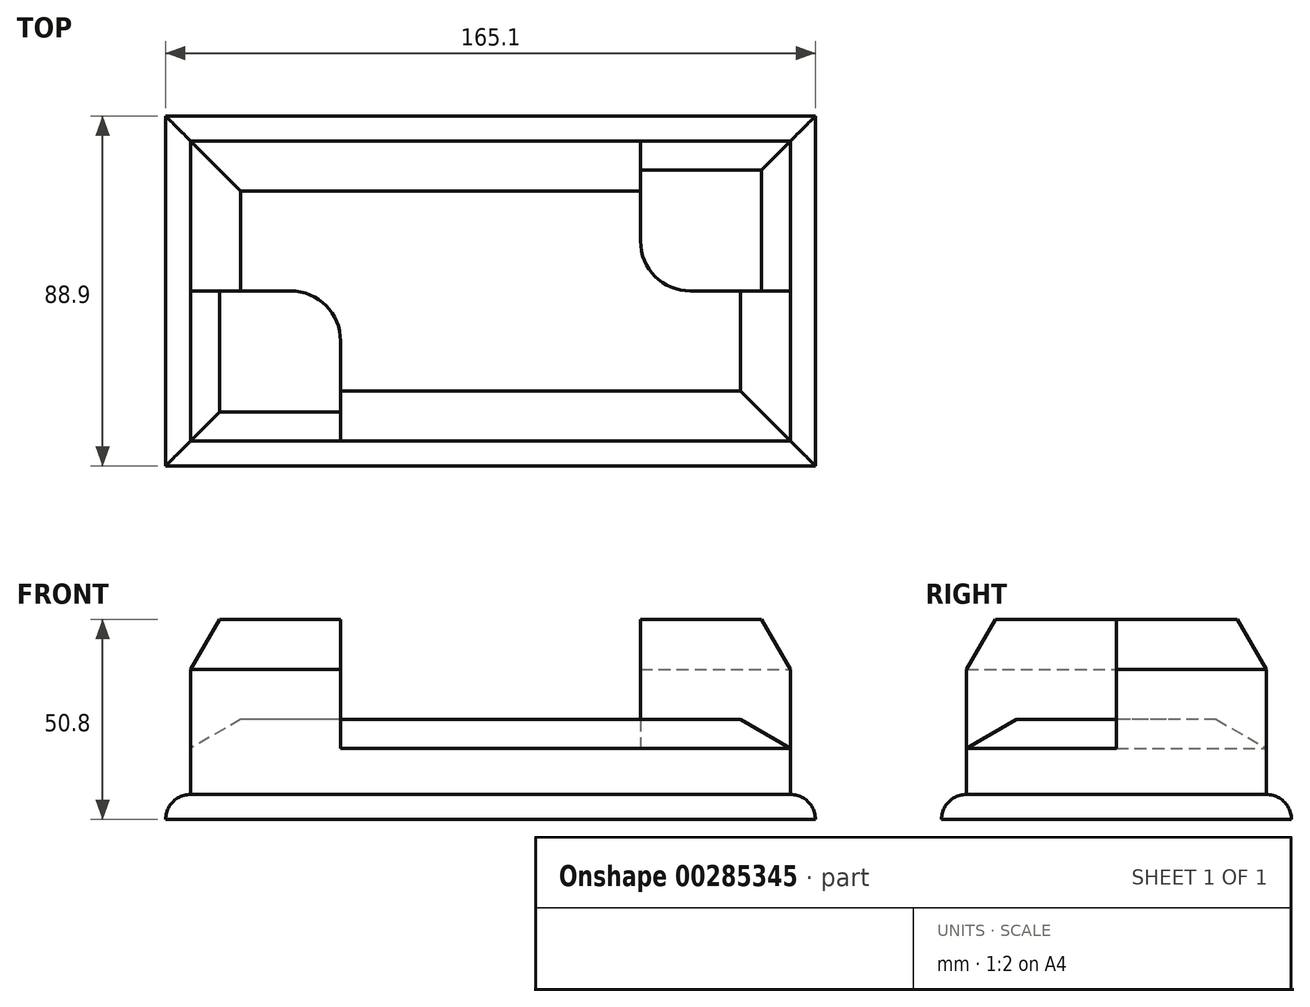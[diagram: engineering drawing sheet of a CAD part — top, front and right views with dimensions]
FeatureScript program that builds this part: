
annotation { "Feature Type Name" : "Feature", "Feature Type Description" : "" }
export const myFeature = defineFeature(function(context is Context, id is Id, definition is map)
    precondition{}
    {
        {
            var Q0;
            Q0=qCreatedBy(makeId("Top.planeOp"),FACE);
            var sketch = newSketch(context, id + "F0", { "sketchPlane" : qUnion([Q0])});
            skLineSegment(sketch, "E0.bottom", {"start": v(-61.87, 51.4) * mm, "end": v(90.53, 51.4) * mm});
            skLineSegment(sketch, "E0.top", {"start": v(-61.87, -24.8) * mm, "end": v(90.53, -24.8) * mm});
            skLineSegment(sketch, "E0.left", {"start": v(-61.87, 51.4) * mm, "end": v(-61.87, -24.8) * mm});
            skLineSegment(sketch, "E0.right", {"start": v(90.53, 51.4) * mm, "end": v(90.53, -24.8) * mm});
            skLineSegment(sketch, "E1.bottom", {"start": v(-36.47, 13.3) * mm, "end": v(-61.87, 13.3) * mm});
            skLineSegment(sketch, "E1.left", {"start": v(-23.77, 0.6) * mm, "end": v(-23.77, -24.8) * mm});
            skLineSegment(sketch, "E2.bottom", {"start": v(-68.22, 57.74) * mm, "end": v(96.88, 57.74) * mm});
            skLineSegment(sketch, "E2.top", {"start": v(-68.22, -31.16) * mm, "end": v(96.88, -31.16) * mm});
            skLineSegment(sketch, "E2.left", {"start": v(-68.22, 57.74) * mm, "end": v(-68.22, -31.16) * mm});
            skLineSegment(sketch, "E2.right", {"start": v(96.88, 57.74) * mm, "end": v(96.88, -31.16) * mm});
            skLineSegment(sketch, "E3.top", {"start": v(90.53, 13.3) * mm, "end": v(65.13, 13.3) * mm});
            skLineSegment(sketch, "E3.right", {"start": v(52.43, 51.4) * mm, "end": v(52.43, 26) * mm});
            skPoint(sketch, "E4.visualSharp", {"position": v(-23.77, 13.3) * mm});
            skArc(sketch, "E4.filletArc", {"start": v(-23.77, 0.6) * mm, "mid": v(-27.5, 9.57) * mm, "end": v(-36.47, 13.3) * mm});
            skPoint(sketch, "E5.visualSharp", {"position": v(52.43, 13.3) * mm});
            skArc(sketch, "E5.filletArc", {"start": v(52.43, 26) * mm, "mid": v(56.15, 17.01) * mm, "end": v(65.13, 13.3) * mm});
            skSolve(sketch);
        }
        {
            var Q0;
            {var subQ7=sQuery(id+"F0.wireOp",EDGE,"E1.bottom");Q0=makeQuery(id+"F0.imprint","IMPRINT",FACE,{"disambiguationData":[TD([[makeQuery(id+"F0.imprint","IMPRINT",EDGE,{"derivedFrom":subQ7}),-1.0]])]});}
            extrude(context, id + "F1", {"entities" : qUnion([Q0]), "depth" : 25.4 * mm});
        }
        {
            var Q0;
            Q0=makeQuery(id+"F0.imprint","IMPRINT",FACE,{"disambiguationData":[TD([[makeQuery(id+"F0.imprint","IMPRINT",EDGE,{"derivedFrom":sQuery(id+"F0.wireOp",EDGE,"E2.bottom")}),-1.0]])]});
            extrude(context, id + "F2", {"entities" : qUnion([Q0]), "operationType" : NewBodyOperationType.ADD, "depth" : 6.35 * mm});
        }
        {
            var Q0;
            {var subQ1=sQuery(id+"F0.wireOp",EDGE,"E1.bottom");Q0=makeQuery(id+"F0.imprint","IMPRINT",FACE,{"disambiguationData":[TD([[makeQuery(id+"F0.imprint","IMPRINT",EDGE,{"derivedFrom":subQ1}),1.0]])]});}
            var Q1;
            {var subQ1=sQuery(id+"F0.wireOp",EDGE,"E3.top");Q1=makeQuery(id+"F0.imprint","IMPRINT",FACE,{"disambiguationData":[TD([[makeQuery(id+"F0.imprint","IMPRINT",EDGE,{"derivedFrom":subQ1}),-1.0]])]});}
            extrude(context, id + "F3", {"entities" : qUnion([Q0, Q1]), "operationType" : NewBodyOperationType.ADD, "depth" : 50.8 * mm});
        }
        {
            var Q0;
            Q0=makeQuery(id+"F3.opExtrude","CAP_EDGE",EDGE,{"disambiguationData":[OSD([sQuery(id+"F0.wireOp",EDGE,"E0.right")])],"isStart":false});
            var Q1;
            Q1=makeQuery(id+"F3.opExtrude","CAP_EDGE",EDGE,{"disambiguationData":[OSD([sQuery(id+"F0.wireOp",EDGE,"E0.bottom")])],"isStart":false});
            chamfer(context, id + "F4", {"entities" : qUnion([Q0, Q1]), "chamferType" : ChamferType.OFFSET_ANGLE, "width" : 12.7 * mm, "oppositeDirection" : false, "angle" : 30 * degree, "tangentPropagation" : true});
        }
        {
            var Q0;
            Q0=makeQuery(id+"F3.opExtrude","CAP_EDGE",EDGE,{"disambiguationData":[OSD([sQuery(id+"F0.wireOp",EDGE,"E0.left")])],"isStart":false});
            var Q1;
            Q1=makeQuery(id+"F3.opExtrude","CAP_EDGE",EDGE,{"disambiguationData":[OSD([sQuery(id+"F0.wireOp",EDGE,"E0.top")])],"isStart":false});
            chamfer(context, id + "F5", {"entities" : qUnion([Q0, Q1]), "chamferType" : ChamferType.OFFSET_ANGLE, "width" : 12.7 * mm, "oppositeDirection" : true, "angle" : 30 * degree, "tangentPropagation" : true});
        }
        {
            var Q0;
            Q0=makeQuery(id+"F1.opExtrude","CAP_EDGE",EDGE,{"disambiguationData":[OSD([sQuery(id+"F0.wireOp",EDGE,"E0.left")])],"isStart":false});
            var Q1;
            Q1=makeQuery(id+"F1.opExtrude","CAP_EDGE",EDGE,{"disambiguationData":[OSD([sQuery(id+"F0.wireOp",EDGE,"E0.bottom")])],"isStart":false});
            var Q2;
            Q2=makeQuery(id+"F1.opExtrude","CAP_EDGE",EDGE,{"disambiguationData":[OSD([sQuery(id+"F0.wireOp",EDGE,"E0.right")])],"isStart":false});
            var Q3;
            Q3=makeQuery(id+"F1.opExtrude","CAP_EDGE",EDGE,{"disambiguationData":[OSD([sQuery(id+"F0.wireOp",EDGE,"E0.top")])],"isStart":false});
            chamfer(context, id + "F6", {"entities" : qUnion([Q0, Q1, Q2, Q3]), "chamferType" : ChamferType.OFFSET_ANGLE, "width" : 12.7 * mm, "oppositeDirection" : false, "angle" : 30 * degree, "tangentPropagation" : true});
        }
        {
            var Q0;
            Q0=makeQuery(id+"F2.opExtrude","CAP_EDGE",EDGE,{"disambiguationData":[OSD([sQuery(id+"F0.wireOp",EDGE,"E2.right")])],"isStart":false});
            var Q1;
            Q1=makeQuery(id+"F2.opExtrude","CAP_EDGE",EDGE,{"disambiguationData":[OSD([sQuery(id+"F0.wireOp",EDGE,"E2.top")])],"isStart":false});
            var Q2;
            Q2=makeQuery(id+"F2.opExtrude","CAP_EDGE",EDGE,{"disambiguationData":[OSD([sQuery(id+"F0.wireOp",EDGE,"E2.bottom")])],"isStart":false});
            var Q3;
            Q3=makeQuery(id+"F2.opExtrude","CAP_EDGE",EDGE,{"disambiguationData":[OSD([sQuery(id+"F0.wireOp",EDGE,"E2.left")])],"isStart":false});
            fillet(context, id + "F7", {"entities" : qUnion([Q0, Q1, Q2, Q3]), "radius" : 6.35 * mm, "tangentPropagation" : true, "allowEdgeOverflow" : false});
        }
    });
